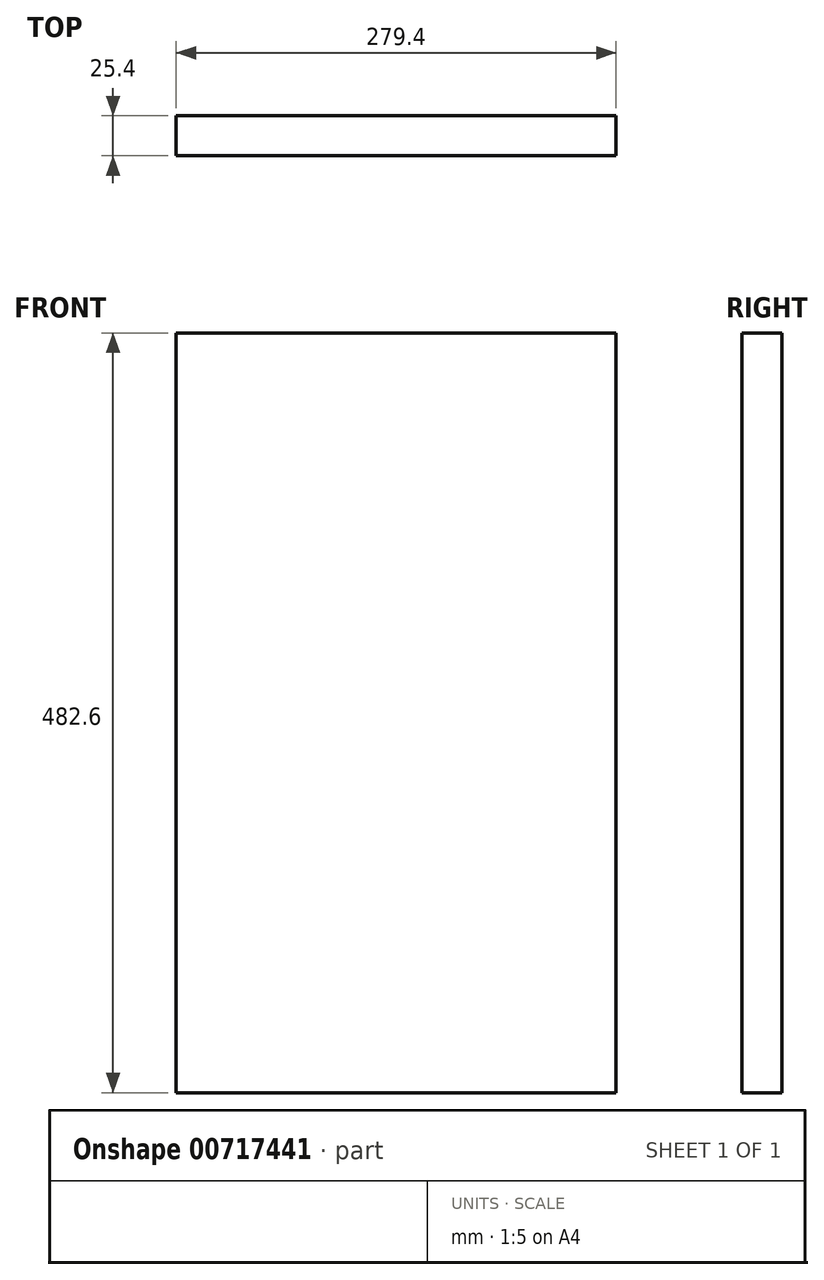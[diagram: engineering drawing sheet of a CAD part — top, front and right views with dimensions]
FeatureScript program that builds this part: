
annotation { "Feature Type Name" : "Feature", "Feature Type Description" : "" }
export const myFeature = defineFeature(function(context is Context, id is Id, definition is map)
    precondition{}
    {
        {
            var Q0;
            Q0=qCreatedBy(makeId("Front.planeOp"),FACE);
            var sketch = newSketch(context, id + "F0", { "sketchPlane" : qUnion([Q0])});
            skLineSegment(sketch, "E0.bottom", {"start": v(0, 0) * mm, "end": v(279.4, 0) * mm});
            skLineSegment(sketch, "E0.top", {"start": v(0, 482.6) * mm, "end": v(279.4, 482.6) * mm});
            skLineSegment(sketch, "E0.left", {"start": v(0, 0) * mm, "end": v(0, 482.6) * mm});
            skLineSegment(sketch, "E0.right", {"start": v(279.4, 0) * mm, "end": v(279.4, 482.6) * mm});
            skSolve(sketch);
        }
        {
            var Q0;
            Q0=makeQuery(id+"F0.imprint","IMPRINT",FACE,{"disambiguationData":[TD([[makeQuery(id+"F0.imprint","IMPRINT",EDGE,{"derivedFrom":sQuery(id+"F0.wireOp",EDGE,"E0.bottom")}),1.0]])]});
            extrude(context, id + "F1", {"entities" : qUnion([Q0]), "depth" : 25.4 * mm, "offsetDistance" : 25.4 * mm});
        }
    });
